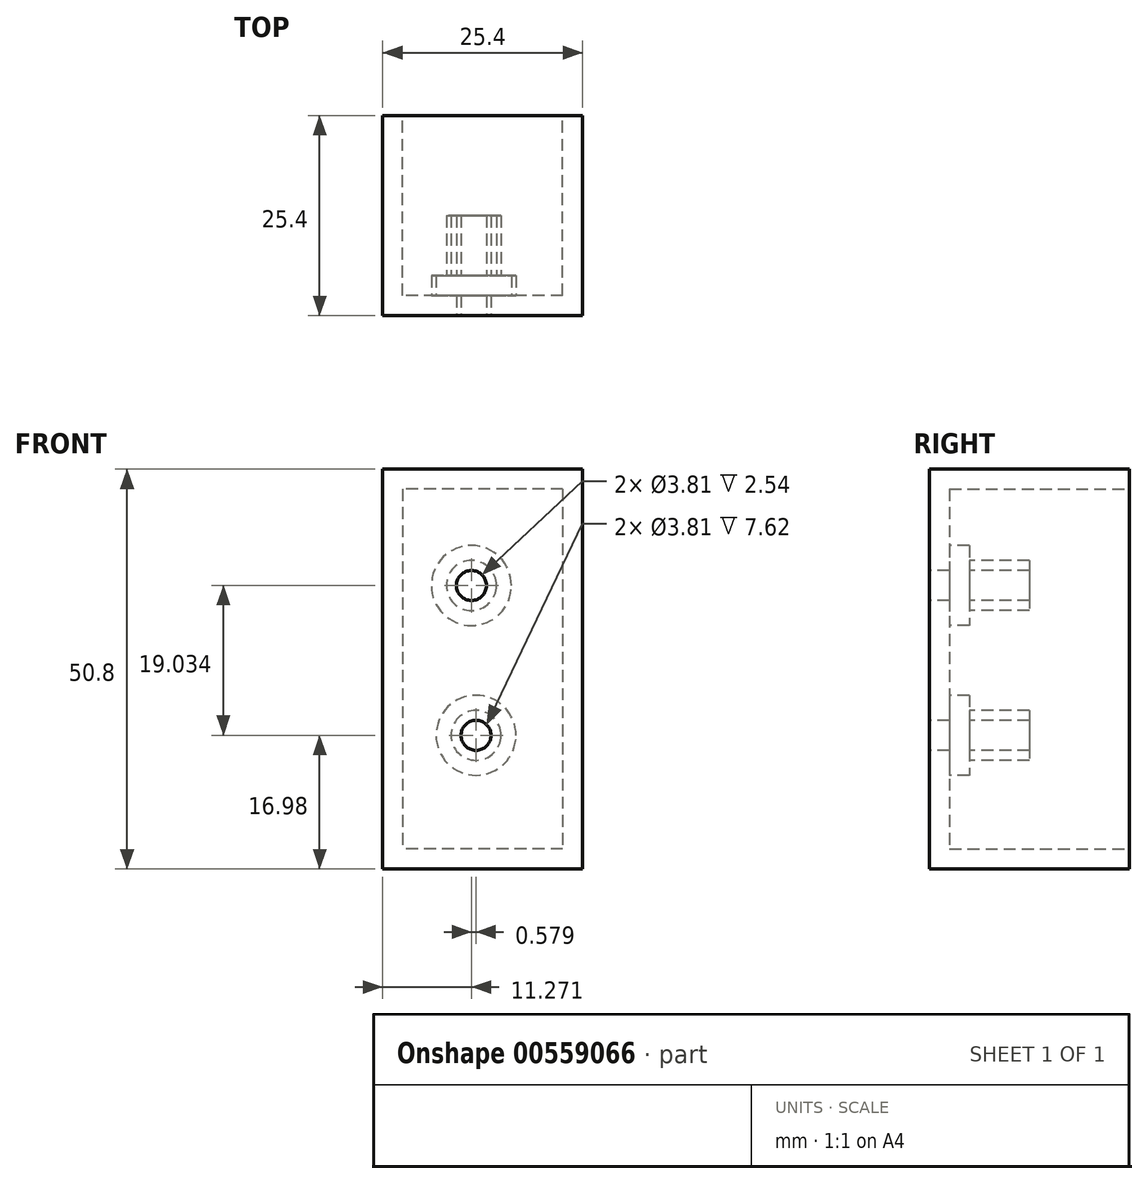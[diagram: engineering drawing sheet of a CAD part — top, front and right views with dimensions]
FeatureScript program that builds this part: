
annotation { "Feature Type Name" : "Feature", "Feature Type Description" : "" }
export const myFeature = defineFeature(function(context is Context, id is Id, definition is map)
    precondition{}
    {
        {
            var Q0;
            Q0=qCreatedBy(makeId("Top.planeOp"),FACE);
            var sketch = newSketch(context, id + "F0", { "sketchPlane" : qUnion([Q0])});
            skLineSegment(sketch, "E0.bottom", {"start": v(-23.22, 6.19) * mm, "end": v(2.18, 6.19) * mm});
            skLineSegment(sketch, "E0.top", {"start": v(-23.22, -19.21) * mm, "end": v(2.18, -19.21) * mm});
            skLineSegment(sketch, "E0.left", {"start": v(-23.22, 6.19) * mm, "end": v(-23.22, -19.21) * mm});
            skLineSegment(sketch, "E0.right", {"start": v(2.18, 6.19) * mm, "end": v(2.18, -19.21) * mm});
            skSolve(sketch);
        }
        {
            var Q0;
            Q0=makeQuery(id+"F0.imprint","IMPRINT",FACE,{"disambiguationData":[TD([[makeQuery(id+"F0.imprint","IMPRINT",EDGE,{"derivedFrom":sQuery(id+"F0.wireOp",EDGE,"E0.bottom")}),-1.0]])]});
            extrude(context, id + "F1", {"entities" : qUnion([Q0]), "depth" : 50.8 * mm, "offsetDistance" : 25.4 * mm});
        }
        {
            var Q0;
            Q0=makeQuery(id+"F1.opExtrude","SWEPT_FACE",FACE,{"disambiguationData":[OSD([sQuery(id+"F0.wireOp",EDGE,"E0.bottom")])]});
            var sketch = newSketch(context, id + "F2", { "sketchPlane" : qUnion([Q0])});
            skLineSegment(sketch, "E1.bottom", {"start": v(0.36, 48.26) * mm, "end": v(20.68, 48.26) * mm});
            skLineSegment(sketch, "E1.top", {"start": v(0.36, 2.54) * mm, "end": v(20.68, 2.54) * mm});
            skLineSegment(sketch, "E1.left", {"start": v(0.36, 48.26) * mm, "end": v(0.36, 2.54) * mm});
            skLineSegment(sketch, "E1.right", {"start": v(20.68, 48.26) * mm, "end": v(20.68, 2.54) * mm});
            skSolve(sketch);
        }
        {
            var Q0;
            Q0=makeQuery(id+"F2.imprint","IMPRINT",FACE,{"disambiguationData":[TD([[makeQuery(id+"F2.imprint","IMPRINT",EDGE,{"derivedFrom":sQuery(id+"F2.wireOp",EDGE,"E1.bottom")}),-1.0]])]});
            extrude(context, id + "F3", {"entities" : qUnion([Q0]), "operationType" : NewBodyOperationType.REMOVE, "oppositeDirection" : true, "depth" : 22.86 * mm, "offsetDistance" : 25.4 * mm});
        }
        {
            var Q0;
            Q0=makeQuery(id+"F3.boolean.opBoolean","COPY",FACE,{"derivedFrom":makeQuery(id+"F3.opExtrude","CAP_FACE",FACE,{"disambiguationData":[OSD([sQuery(id+"F2.wireOp",EDGE,"E1.bottom"),sQuery(id+"F2.wireOp",EDGE,"E1.top"),sQuery(id+"F2.wireOp",EDGE,"E1.left"),sQuery(id+"F2.wireOp",EDGE,"E1.right")])],"isStart":false})});
            var sketch = newSketch(context, id + "F4", { "sketchPlane" : qUnion([Q0])});
            skCircle(sketch, "E2", {"center": v(11.95, 36.01) * mm, "radius": 1.9 * mm});
            skCircle(sketch, "E3", {"center": v(11.95, 36.01) * mm, "radius": 3.18 * mm});
            skCircle(sketch, "E4", {"center": v(11.37, 16.98) * mm, "radius": 1.9 * mm});
            skCircle(sketch, "E5", {"center": v(11.37, 16.98) * mm, "radius": 3.18 * mm});
            skSolve(sketch);
        }
        {
            var Q0;
            Q0 = qSketchRegion(id + "F4", true);
            extrude(context, id + "F5", {"entities" : qUnion([Q0]), "operationType" : NewBodyOperationType.ADD, "depth" : 10.16 * mm, "offsetDistance" : 25.4 * mm});
        }
        {
            var Q0;
            Q0=makeQuery(id+"F5.boolean.opBoolean","SPLIT",FACE,{"disambiguationData":[TD([makeQuery(id+"F5.opExtrude","SWEPT_FACE",FACE,{"disambiguationData":[OSD([sQuery(id+"F4.wireOp",EDGE,"E2")])]})])],"derivedFrom":makeQuery(id+"F3.boolean.opBoolean","COPY",FACE,{"derivedFrom":makeQuery(id+"F3.opExtrude","CAP_FACE",FACE,{"disambiguationData":[OSD([sQuery(id+"F2.wireOp",EDGE,"E1.bottom"),sQuery(id+"F2.wireOp",EDGE,"E1.top"),sQuery(id+"F2.wireOp",EDGE,"E1.left"),sQuery(id+"F2.wireOp",EDGE,"E1.right")])],"isStart":false})})});
            var Q1;
            Q1=makeQuery(id+"F5.boolean.opBoolean","SPLIT",FACE,{"disambiguationData":[TD([makeQuery(id+"F5.opExtrude","SWEPT_FACE",FACE,{"disambiguationData":[OSD([sQuery(id+"F4.wireOp",EDGE,"E4")])]})])],"derivedFrom":makeQuery(id+"F3.boolean.opBoolean","COPY",FACE,{"derivedFrom":makeQuery(id+"F3.opExtrude","CAP_FACE",FACE,{"disambiguationData":[OSD([sQuery(id+"F2.wireOp",EDGE,"E1.bottom"),sQuery(id+"F2.wireOp",EDGE,"E1.top"),sQuery(id+"F2.wireOp",EDGE,"E1.left"),sQuery(id+"F2.wireOp",EDGE,"E1.right")])],"isStart":false})})});
            extrude(context, id + "F6", {"entities" : qUnion([Q0, Q1]), "operationType" : NewBodyOperationType.REMOVE, "oppositeDirection" : true, "depth" : 25.4 * mm, "offsetDistance" : 25.4 * mm});
        }
        {
            var Q0;
            {var subQ0=sQuery(id+"F2.wireOp",EDGE,"E1.right");var subQ1=sQuery(id+"F2.wireOp",EDGE,"E1.left");var subQ2=sQuery(id+"F2.wireOp",EDGE,"E1.top");var subQ3=sQuery(id+"F2.wireOp",EDGE,"E1.bottom");Q0=makeQuery(id+"F5.boolean.opBoolean","SPLIT",FACE,{"disambiguationData":[TD([makeQuery(id+"F3.boolean.opBoolean","COPY",FACE,{"derivedFrom":makeQuery(id+"F3.opExtrude","SWEPT_FACE",FACE,{"disambiguationData":[OSD([subQ3])]})})])],"derivedFrom":makeQuery(id+"F3.boolean.opBoolean","COPY",FACE,{"derivedFrom":makeQuery(id+"F3.opExtrude","CAP_FACE",FACE,{"disambiguationData":[OSD([subQ3,subQ2,subQ1,subQ0])],"isStart":false})})});}
            var sketch = newSketch(context, id + "F7", { "sketchPlane" : qUnion([Q0])});
            skCircle(sketch, "E6", {"center": v(11.37, 16.98) * mm, "radius": 5.08 * mm});
            skCircle(sketch, "E7", {"center": v(11.95, 36.01) * mm, "radius": 5.08 * mm});
            skSolve(sketch);
        }
        {
            var Q0;
            Q0 = qSketchRegion(id + "F7", true);
            extrude(context, id + "F8", {"entities" : qUnion([Q0]), "operationType" : NewBodyOperationType.ADD, "depth" : 2.54 * mm, "offsetDistance" : 25.4 * mm});
        }
    });
